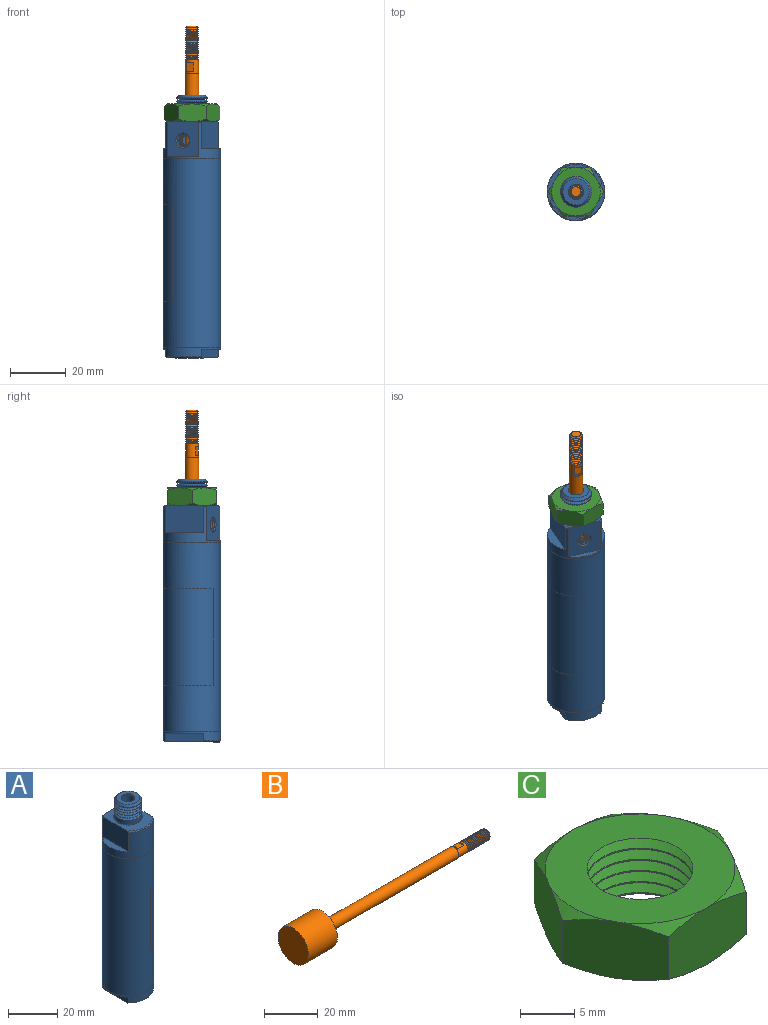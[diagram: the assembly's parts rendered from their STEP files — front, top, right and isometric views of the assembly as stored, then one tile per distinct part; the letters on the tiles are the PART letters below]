
ASSEMBLY  parts=3 mates=4
PART A: 146 faces, bbox 20.7x20.7x94.8 mm
  f0: cylinder r=7.96mm len=54.98mm, axis (0,0,-1), area 2750.9mm2, adj f46,f108
  f1: plane 9.12x9.12mm, normal (0,0,1), area 51.8mm2, adj f2,f11
  f2: cone r=4.7mm half-angle=45deg, axis (0,0,-1), area 11.7mm2, adj f1,f47
  f3: cone r=10.08mm half-angle=45deg, axis (0,0,1), area 9.7mm2, adj f5,f6,f8,f10
  f4: cone r=10.08mm half-angle=45deg, axis (0,0,1), area 9.7mm2, adj f5,f6,f8,f10
  f5: plane 19.72x14mm, normal (0,0,-1), area 226.4mm2, adj f3,f4,f8,f10,f12
  f6: cylinder r=10.31mm len=20.61mm, axis (0,0,-1), area 133.4mm2, adj f3,f4,f7,f8,f9,f10,f117
  f7: plane 15.13x3.31mm, normal (0,0,-1), area 34.6mm2, adj f6,f8
  f8: plane 15.15x3.19mm, normal (-1,0,0), area 47.8mm2, adj f3,f4,f5,f6,f7
  f9: plane 15.13x3.31mm, normal (0,0,-1), area 34.6mm2, adj f6,f10
  f10: plane 15.15x3.19mm, normal (1,0,0), area 47.8mm2, adj f3,f4,f5,f6,f9
  f11: cylinder r=2.07mm len=4.14mm, axis (0,0,1), area 3.1mm2, adj f1,f44
  f12: cone r=2.78mm half-angle=45deg, axis (0,0,-1), area 15.3mm2, adj f5,f13
  f13: cone r=2.37mm half-angle=60deg, axis (0,0,1), area 10.4mm2, adj f12,f14
  f14: cone r=2.37mm half-angle=60deg, axis (0,0,-1), area 10.4mm2, adj f13,f24
  f15: cylinder r=2.07mm len=4.14mm, axis (0,0,1), area 1.1mm2, adj f42,f43
  f16: cylinder r=2.07mm len=4.14mm, axis (0,0,1), area 1.1mm2, adj f40,f41
  f17: cylinder r=2.07mm len=4.14mm, axis (0,0,1), area 1.1mm2, adj f38,f39
  f18: cylinder r=2.07mm len=4.14mm, axis (0,0,1), area 1.1mm2, adj f36,f37
  f19: cylinder r=2.07mm len=4.14mm, axis (0,0,1), area 1.1mm2, adj f34,f35
  f20: cylinder r=2.07mm len=4.14mm, axis (0,0,1), area 1.1mm2, adj f32,f33
  f21: cylinder r=2.07mm len=4.14mm, axis (0,0,1), area 1.1mm2, adj f30,f31
  f22: cylinder r=2.07mm len=4.14mm, axis (0,0,1), area 1.1mm2, adj f28,f29
  f23: cylinder r=2.07mm len=4.14mm, axis (0,0,1), area 1.1mm2, adj f26,f27
  f24: cylinder r=2.07mm len=4.14mm, axis (0,0,1), area 1.1mm2, adj f14,f25
  f25: cone r=2.37mm half-angle=60deg, axis (0,0,1), area 10.4mm2, adj f24,f26
  f26: cone r=2.37mm half-angle=60deg, axis (0,0,-1), area 10.4mm2, adj f23,f25
  f27: cone r=2.37mm half-angle=60deg, axis (0,0,1), area 10.4mm2, adj f23,f28
  f28: cone r=2.37mm half-angle=60deg, axis (0,0,-1), area 10.4mm2, adj f22,f27
  f29: cone r=2.37mm half-angle=60deg, axis (0,0,1), area 10.4mm2, adj f22,f30
  f30: cone r=2.37mm half-angle=60deg, axis (0,0,-1), area 10.4mm2, adj f21,f29
  f31: cone r=2.37mm half-angle=60deg, axis (0,0,1), area 10.4mm2, adj f21,f32
  f32: cone r=2.37mm half-angle=60deg, axis (0,0,-1), area 10.4mm2, adj f20,f31
  f33: cone r=2.37mm half-angle=60deg, axis (0,0,1), area 10.4mm2, adj f20,f34
  f34: cone r=2.37mm half-angle=60deg, axis (0,0,-1), area 10.4mm2, adj f19,f33
  f35: cone r=2.37mm half-angle=60deg, axis (0,0,1), area 10.4mm2, adj f19,f36
  f36: cone r=2.37mm half-angle=60deg, axis (0,0,-1), area 10.4mm2, adj f18,f35
  f37: cone r=2.37mm half-angle=60deg, axis (0,0,1), area 10.4mm2, adj f18,f38
  f38: cone r=2.37mm half-angle=60deg, axis (0,0,-1), area 10.4mm2, adj f17,f37
  f39: cone r=2.37mm half-angle=60deg, axis (0,0,1), area 10.4mm2, adj f17,f40
  f40: cone r=2.37mm half-angle=60deg, axis (0,0,-1), area 10.4mm2, adj f16,f39
  f41: cone r=2.37mm half-angle=60deg, axis (0,0,1), area 10.4mm2, adj f16,f42
  f42: cone r=2.37mm half-angle=60deg, axis (0,0,-1), area 10.4mm2, adj f15,f41
  f43: cone r=2.37mm half-angle=60deg, axis (0,0,1), area 10.4mm2, adj f15,f44
  f44: cone r=2.37mm half-angle=60deg, axis (0,0,-1), area 10.4mm2, adj f11,f43
  f45: plane 15.42x15.42mm, normal (0,0,1), area 113.1mm2, adj f46,f47
  f46: cone r=7.84mm half-angle=30deg, axis (0,0,-1), area 25mm2, adj f0,f45
  f47: cylinder r=4.84mm len=9.68mm, axis (0,0,-1), area 47.1mm2, adj f2,f45
  f48: cylinder r=2.77mm len=5.54mm, axis (0,0,1), area 10mm2, adj f54,f113
  f49: plane 6x6mm, normal (0,0,-1), area 0.1mm2, adj f50,f111
  f50: cylinder r=3mm len=9.84mm, axis (0,0,1), area 185.5mm2, adj f49,f51
  f51: cone r=3.13mm half-angle=45deg, axis (0,0,-1), area 7.1mm2, adj f50,f52
  f52: plane 7.52x7.52mm, normal (0,0,-1), area 11.1mm2, adj f51,f53
  f53: torus R=3.76mm, axis (0,0,1), area 7.8mm2, adj f52,f79
  f54: plane 9.46x9.46mm, normal (0,0,1), area 46.2mm2, adj f48,f55
  f55: cone r=5.14mm half-angle=45deg, axis (0,0,-1), area 37.7mm2, adj f54,f57
  f56: cone r=10.08mm half-angle=45deg, axis (0,0,-1), area 9.9mm2, adj f58,f64,f65,f68
  f57: cylinder r=5.56mm len=11.11mm, axis (0,0,-1), area 12.3mm2, adj f55,f105
  f58: plane 18.12x14.17mm, normal (0,0,1), area 137.2mm2, adj f56,f59,f62,f64,f65,f67,f69
  f59: torus R=5.76mm, axis (0,0,-1), area 11.3mm2, adj f58,f92
  f60: plane 9.12x9.12mm, normal (0,0,-1), area 16mm2, adj f61,f79
  f61: cone r=4.7mm half-angle=45deg, axis (0,0,1), area 11.7mm2, adj f60,f109
  f62: cone r=10.08mm half-angle=45deg, axis (0,0,-1), area 1.1mm2, adj f58,f65,f68,f69
  f63: plane 14.97x3.22mm, normal (0,0,1), area 33.3mm2, adj f64,f68
  f64: plane 14.98x9.9mm, normal (1,0,0), area 147.6mm2, adj f56,f58,f63,f67,f68
  f65: plane 14.98x9.9mm, normal (-1,0,0), area 147.6mm2, adj f56,f58,f62,f66,f68
  f66: plane 14.97x3.22mm, normal (0,0,1), area 33.3mm2, adj f65,f68
  f67: cone r=10.08mm half-angle=45deg, axis (0,0,-1), area 1.1mm2, adj f58,f64,f68,f69
  f68: cylinder r=10.31mm len=20.61mm, axis (0,0,-1), area 364.7mm2, adj f56,f62,f63,f64,f65,f66,f67,f69
  f69: plane 12.72x12.36mm, normal (0,1,0), area 132.1mm2, adj f58,f62,f67,f68,f70,f72
  f70: plane 12.34x2.05mm, normal (0,0,1), area 17.2mm2, adj f68,f69
  f71: cylinder r=2.07mm len=4.14mm, axis (0,-1,0), area 1.1mm2, adj f79,f87,f88,f89
  f72: cone r=2.78mm half-angle=45deg, axis (0,1,0), area 11mm2, adj f69,f73
  f73: cone r=2.37mm half-angle=60deg, axis (0,-1,0), area 6.9mm2, adj f72,f74
  f74: cone r=2.37mm half-angle=60deg, axis (0,1,0), area 10.4mm2, adj f73,f78
  f75: cylinder r=2.07mm len=4.14mm, axis (0,-1,0), area 1.1mm2, adj f85,f86
  f76: cylinder r=2.07mm len=4.14mm, axis (0,-1,0), area 1.1mm2, adj f83,f84
  f77: cylinder r=2.07mm len=4.14mm, axis (0,-1,0), area 1.1mm2, adj f81,f82
  f78: cylinder r=2.07mm len=4.14mm, axis (0,-1,0), area 1.1mm2, adj f74,f80
  f79: cylinder r=3.96mm len=17.7mm, axis (0,0,1), area 423.2mm2, adj f53,f60,f71,f88,f89,f90,f91
  f80: cone r=2.37mm half-angle=60deg, axis (0,-1,0), area 10.4mm2, adj f78,f81
  f81: cone r=2.37mm half-angle=60deg, axis (0,1,0), area 10.4mm2, adj f77,f80
  f82: cone r=2.37mm half-angle=60deg, axis (0,-1,0), area 10.4mm2, adj f77,f83
  f83: cone r=2.37mm half-angle=60deg, axis (0,1,0), area 10.4mm2, adj f76,f82
  f84: cone r=2.37mm half-angle=60deg, axis (0,-1,0), area 10.4mm2, adj f76,f85
  f85: cone r=2.37mm half-angle=60deg, axis (0,1,0), area 10.4mm2, adj f75,f84
  f86: cone r=2.37mm half-angle=60deg, axis (0,-1,0), area 10.4mm2, adj f75,f87
  f87: cone r=2.37mm half-angle=60deg, axis (0,1,0), area 10.4mm2, adj f71,f86
  f88: cone r=2.37mm half-angle=60deg, axis (0,-1,0), area 3.9mm2, adj f71,f79,f90
  f89: cone r=2.37mm half-angle=60deg, axis (0,-1,0), area 3.9mm2, adj f71,f79,f91
  f90: cone r=2.37mm half-angle=60deg, axis (0,1,0), area 1.8mm2, adj f79,f88
  f91: cone r=2.37mm half-angle=60deg, axis (0,1,0), area 1.8mm2, adj f79,f89
  f92: cylinder r=5.56mm len=11.11mm, axis (0,0,-1), area 70.9mm2, adj f59,f94
  f93: cone r=5.08mm half-angle=60deg, axis (0,0,1), area 35.4mm2, adj f94,f98
  f94: cone r=5.08mm half-angle=60deg, axis (0,0,-1), area 35.4mm2, adj f92,f93
  f95: cylinder r=5.56mm len=11.11mm, axis (0,0,-1), area 4.8mm2, adj f103,f106
  f96: cylinder r=5.56mm len=11.11mm, axis (0,0,-1), area 4.8mm2, adj f101,f104
  f97: cylinder r=5.56mm len=11.11mm, axis (0,0,-1), area 4.8mm2, adj f99,f102
  f98: cylinder r=5.56mm len=11.11mm, axis (0,0,-1), area 4.8mm2, adj f93,f100
  f99: cone r=5.08mm half-angle=60deg, axis (0,0,1), area 35.4mm2, adj f97,f100
  f100: cone r=5.08mm half-angle=60deg, axis (0,0,-1), area 35.4mm2, adj f98,f99
  f101: cone r=5.08mm half-angle=60deg, axis (0,0,1), area 35.4mm2, adj f96,f102
  f102: cone r=5.08mm half-angle=60deg, axis (0,0,-1), area 35.4mm2, adj f97,f101
  f103: cone r=5.08mm half-angle=60deg, axis (0,0,1), area 35.4mm2, adj f95,f104
  f104: cone r=5.08mm half-angle=60deg, axis (0,0,-1), area 35.4mm2, adj f96,f103
  f105: cone r=5.08mm half-angle=60deg, axis (0,0,1), area 35.4mm2, adj f57,f106
  f106: cone r=5.08mm half-angle=60deg, axis (0,0,-1), area 35.4mm2, adj f95,f105
  f107: plane 15.42x15.42mm, normal (0,0,-1), area 113.1mm2, adj f108,f109
  f108: cone r=7.84mm half-angle=30deg, axis (0,0,1), area 25mm2, adj f0,f107
  f109: cylinder r=4.84mm len=9.68mm, axis (0,0,1), area 47.1mm2, adj f61,f107
  f110: plane 5.99x5.99mm, normal (0,0,-1), area 8mm2, adj f111,f112
  f111: cylinder r=3mm len=9.53mm, axis (0,0,-1), area 179.4mm2, adj f49,f110
  f112: cylinder r=2.54mm len=9.53mm, axis (0,0,-1), area 152mm2, adj f110,f113
  f113: plane 5.54x5.54mm, normal (0,0,1), area 3.9mm2, adj f48,f112
  f114: cylinder r=10.36mm len=67.82mm, axis (0,0,1), area 3509.3mm2, adj f115,f116,f117
  f115: cylinder r=10.36mm len=34.93mm, axis (0,0,1), area 906.6mm2, adj f114
  f116: plane 20.73x20.73mm, normal (0,0,1), area 3.7mm2, adj f68,f114
  f117: plane 20.73x20.73mm, normal (0,0,-1), area 3.7mm2, adj f6,f114
  f118: plane 18.49x18.49mm, normal (0,0,-1), area 69.3mm2, adj f119,f125
  f119: cylinder r=9.25mm len=59.06mm, axis (0,0,-1), area 3430.6mm2, adj f118,f120
  f120: plane 18.49x18.49mm, normal (0,0,1), area 69.3mm2, adj f119,f130
  f121: cone r=9.61mm half-angle=30deg, axis (0,0,-1), area 16mm2, adj f122,f131
  f122: plane 19.04x19.04mm, normal (0,0,1), area 22mm2, adj f121,f123
  f123: cylinder r=9.14mm len=18.29mm, axis (0,0,-1), area 43.8mm2, adj f122,f124
  f124: plane 18.29x18.29mm, normal (0,0,1), area 63.5mm2, adj f123,f125
  f125: cylinder r=7.96mm len=15.93mm, axis (0,0,-1), area 15.9mm2, adj f118,f124
  f126: plane 19.04x19.04mm, normal (0,0,-1), area 22mm2, adj f127,f128
  f127: cone r=9.61mm half-angle=30deg, axis (0,0,1), area 16mm2, adj f126,f131
  f128: cylinder r=9.14mm len=18.29mm, axis (0,0,1), area 43.8mm2, adj f126,f129
  f129: plane 18.29x18.29mm, normal (0,0,-1), area 63.5mm2, adj f128,f130
  f130: cylinder r=7.96mm len=15.93mm, axis (0,0,1), area 15.9mm2, adj f120,f129
  f131: cylinder r=9.65mm len=61.67mm, axis (0,0,1), area 3740.2mm2, adj f121,f127
  f132: cylinder r=9.65mm len=19.3mm, axis (0,0,1), area 81.1mm2, adj f133,f138
  f133: cone r=9.78mm half-angle=30deg, axis (0,0,1), area 31.2mm2, adj f132,f139
  f134: torus R=9.33mm, axis (0,0,1), area 15.1mm2, adj f135,f136
  f135: cylinder r=9.13mm len=18.26mm, axis (0,0,-1), area 72.2mm2, adj f134,f137
  f136: cone r=9.42mm half-angle=74deg, axis (0,0,1), area 26.3mm2, adj f134,f139
  f137: torus R=9.33mm, axis (0,0,-1), area 18.5mm2, adj f135,f138
  f138: plane 19.3x19.3mm, normal (0,0,1), area 18.9mm2, adj f132,f137
  f139: plane 19.81x19.81mm, normal (0,0,-1), area 12.5mm2, adj f133,f136
  f140: cylinder r=9.65mm len=19.3mm, axis (0,0,1), area 81.1mm2, adj f141,f145
  f141: cone r=9.78mm half-angle=30deg, axis (0,0,-1), area 31.2mm2, adj f140,f144
  f142: cone r=9.42mm half-angle=74deg, axis (0,0,-1), area 35.2mm2, adj f143,f144
  f143: cylinder r=9.13mm len=18.26mm, axis (0,0,-1), area 92.6mm2, adj f142,f145
  f144: plane 19.81x19.81mm, normal (0,0,1), area 12.5mm2, adj f141,f142
  f145: plane 19.3x19.3mm, normal (0,0,-1), area 30.7mm2, adj f140,f143
PART B: 59 faces, bbox 101.7x15.9x15.9 mm
  f0: cone r=2.06mm half-angle=60deg, axis (1,0,0), area 9mm2, adj f1,f43
  f1: cone r=2.06mm half-angle=60deg, axis (-1,0,0), area 9mm2, adj f0,f49
  f2: cone r=2.06mm half-angle=60deg, axis (1,0,0), area 9mm2, adj f3,f42
  f3: cone r=2.06mm half-angle=60deg, axis (-1,0,0), area 9mm2, adj f2,f43
  f4: cone r=2.06mm half-angle=60deg, axis (1,0,0), area 9mm2, adj f5,f41
  f5: cone r=2.06mm half-angle=60deg, axis (-1,0,0), area 9mm2, adj f4,f42
  f6: cone r=2.06mm half-angle=60deg, axis (1,0,0), area 9mm2, adj f7,f40
  f7: cone r=2.06mm half-angle=60deg, axis (-1,0,0), area 9mm2, adj f6,f41
  f8: cone r=2.06mm half-angle=60deg, axis (1,0,0), area 9mm2, adj f9,f39
  f9: cone r=2.06mm half-angle=60deg, axis (-1,0,0), area 9mm2, adj f8,f40
  f10: cone r=2.06mm half-angle=60deg, axis (1,0,0), area 9mm2, adj f11,f38
  f11: cone r=2.06mm half-angle=60deg, axis (-1,0,0), area 9mm2, adj f10,f39
  f12: cone r=2.06mm half-angle=60deg, axis (1,0,0), area 9mm2, adj f13,f37
  f13: cone r=2.06mm half-angle=60deg, axis (-1,0,0), area 9mm2, adj f12,f38
  f14: cone r=2.06mm half-angle=60deg, axis (1,0,0), area 9mm2, adj f15,f36
  f15: cone r=2.06mm half-angle=60deg, axis (-1,0,0), area 9mm2, adj f14,f37
  f16: cone r=2.06mm half-angle=60deg, axis (1,0,0), area 9mm2, adj f17,f35
  f17: cone r=2.06mm half-angle=60deg, axis (-1,0,0), area 9mm2, adj f16,f36
  f18: cone r=2.06mm half-angle=60deg, axis (1,0,0), area 9mm2, adj f19,f34
  f19: cone r=2.06mm half-angle=60deg, axis (-1,0,0), area 9mm2, adj f18,f35
  f20: cone r=2.06mm half-angle=60deg, axis (1,0,0), area 9mm2, adj f21,f33
  f21: cone r=2.06mm half-angle=60deg, axis (-1,0,0), area 9mm2, adj f20,f34
  f22: cone r=2.06mm half-angle=60deg, axis (1,0,0), area 9mm2, adj f23,f32
  f23: cone r=2.06mm half-angle=60deg, axis (-1,0,0), area 9mm2, adj f22,f33
  f24: cone r=2.06mm half-angle=60deg, axis (1,0,0), area 9mm2, adj f25,f31
  f25: cone r=2.06mm half-angle=60deg, axis (-1,0,0), area 9mm2, adj f24,f32
  f26: cone r=2.06mm half-angle=60deg, axis (1,0,0), area 9mm2, adj f27,f30
  f27: cone r=2.06mm half-angle=60deg, axis (-1,0,0), area 9mm2, adj f26,f31
  f28: cone r=2.06mm half-angle=60deg, axis (1,0,0), area 7.5mm2, adj f29,f48
  f29: cone r=2.06mm half-angle=60deg, axis (-1,0,0), area 9mm2, adj f28,f30
  f30: cylinder r=2.36mm len=4.72mm, axis (1,0,0), area 1.3mm2, adj f26,f29
  f31: cylinder r=2.36mm len=4.72mm, axis (1,0,0), area 1.3mm2, adj f24,f27
  f32: cylinder r=2.36mm len=4.72mm, axis (1,0,0), area 1.3mm2, adj f22,f25
  f33: cylinder r=2.36mm len=4.72mm, axis (1,0,0), area 1.3mm2, adj f20,f23
  f34: cylinder r=2.36mm len=4.72mm, axis (1,0,0), area 1.3mm2, adj f18,f21
  f35: cylinder r=2.36mm len=4.72mm, axis (1,0,0), area 1.3mm2, adj f16,f19
  f36: cylinder r=2.36mm len=4.72mm, axis (1,0,0), area 1.3mm2, adj f14,f17
  f37: cylinder r=2.36mm len=4.72mm, axis (1,0,0), area 1.3mm2, adj f12,f15
  f38: cylinder r=2.36mm len=4.72mm, axis (1,0,0), area 1.3mm2, adj f10,f13
  f39: cylinder r=2.36mm len=4.72mm, axis (1,0,0), area 1.3mm2, adj f8,f11
  f40: cylinder r=2.36mm len=4.72mm, axis (1,0,0), area 1.3mm2, adj f6,f9
  f41: cylinder r=2.36mm len=4.72mm, axis (1,0,0), area 1.3mm2, adj f4,f7
  f42: cylinder r=2.36mm len=4.72mm, axis (1,0,0), area 1.3mm2, adj f2,f5
  f43: cylinder r=2.36mm len=4.72mm, axis (1,0,0), area 1.3mm2, adj f0,f3
  f44: cone r=2.06mm half-angle=60deg, axis (-1,0,0), area 0.9mm2, adj f48,f50
  f45: plane 15.93x15.93mm, normal (1,0,0), area 179.5mm2, adj f46,f57
  f46: cylinder r=7.96mm len=15.93mm, axis (1,0,0), area 768.8mm2, adj f45,f47
  f47: plane 15.93x15.93mm, normal (-1,0,0), area 199.2mm2, adj f46
  f48: cone r=2.08mm half-angle=45deg, axis (-1,0,0), area 8.1mm2, adj f28,f44
  f49: cylinder r=2.36mm len=4.95mm, axis (1,0,0), area 55.8mm2, adj f1,f51,f52,f53,f54,f55,f56,f58
  f50: plane 3.52x3.52mm, normal (1,0,0), area 9.7mm2, adj f44
  f51: plane 2.63x0.4mm, normal (-1,0,0), area 0.7mm2, adj f49,f53
  f52: plane 2.63x0.4mm, normal (1,0,0), area 0.7mm2, adj f49,f53
  f53: plane 3.18x2.63mm, normal (0,0,1), area 8.4mm2, adj f49,f51,f52
  f54: plane 2.63x0.4mm, normal (1,0,0), area 0.7mm2, adj f49,f56
  f55: plane 2.63x0.4mm, normal (-1,0,0), area 0.7mm2, adj f49,f56
  f56: plane 3.18x2.63mm, normal (0,0,-1), area 8.4mm2, adj f49,f54,f55
  f57: cylinder r=2.5mm len=69.34mm, axis (1,0,0), area 1089.7mm2, adj f45,f58
  f58: plane 5x5mm, normal (1,0,0), area 2.1mm2, adj f49,f57
PART C: 36 faces, bbox 20.2x20.2x6.4 mm
  f0: cone r=5.35mm half-angle=60deg, axis (0,0,-1), area 6.2mm2, adj f31,f32
  f1: cone r=5.35mm half-angle=60deg, axis (0,0,1), area 37.3mm2, adj f2,f31
  f2: cone r=5.35mm half-angle=60deg, axis (0,0,-1), area 37.3mm2, adj f1,f12
  f3: cone r=5.35mm half-angle=60deg, axis (0,0,1), area 37.3mm2, adj f4,f12
  f4: cone r=5.35mm half-angle=60deg, axis (0,0,-1), area 37.3mm2, adj f3,f11
  f5: cone r=5.35mm half-angle=60deg, axis (0,0,1), area 37.3mm2, adj f6,f11
  f6: cone r=5.35mm half-angle=60deg, axis (0,0,-1), area 37.3mm2, adj f5,f10
  f7: cone r=5.35mm half-angle=60deg, axis (0,0,1), area 37.3mm2, adj f8,f10
  f8: cone r=5.35mm half-angle=60deg, axis (0,0,-1), area 37.3mm2, adj f7,f9
  f9: cylinder r=4.86mm len=9.73mm, axis (0,0,-1), area 4.2mm2, adj f8,f13
  f10: cylinder r=4.86mm len=9.73mm, axis (0,0,-1), area 4.2mm2, adj f6,f7
  f11: cylinder r=4.86mm len=9.73mm, axis (0,0,-1), area 4.2mm2, adj f4,f5
  f12: cylinder r=4.86mm len=9.73mm, axis (0,0,-1), area 4.2mm2, adj f2,f3
  f13: cone r=5.35mm half-angle=60deg, axis (0,0,1), area 37.3mm2, adj f9,f14
  f14: cone r=5.35mm half-angle=60deg, axis (0,0,-1), area 37.3mm2, adj f13,f35
  f15: cone r=9.41mm half-angle=60deg, axis (0,0,1), area 4.7mm2, adj f29,f30,f32
  f16: cone r=9.41mm half-angle=60deg, axis (0,0,1), area 4.7mm2, adj f29,f32,f34
  f17: cone r=9.41mm half-angle=60deg, axis (0,0,1), area 4.7mm2, adj f28,f30,f32
  f18: cone r=9.41mm half-angle=60deg, axis (0,0,1), area 4.7mm2, adj f32,f33,f34
  f19: cone r=9.41mm half-angle=60deg, axis (0,0,1), area 4.7mm2, adj f27,f28,f32
  f20: cone r=9.41mm half-angle=60deg, axis (0,0,1), area 4.7mm2, adj f27,f32,f33
  f21: cone r=9.41mm half-angle=60deg, axis (0,0,-1), area 4.7mm2, adj f28,f30,f35
  f22: cone r=9.41mm half-angle=60deg, axis (0,0,-1), area 4.7mm2, adj f29,f30,f35
  f23: cone r=9.41mm half-angle=60deg, axis (0,0,-1), area 4.7mm2, adj f29,f34,f35
  f24: cone r=9.41mm half-angle=60deg, axis (0,0,-1), area 4.7mm2, adj f27,f28,f35
  f25: cone r=9.41mm half-angle=60deg, axis (0,0,-1), area 4.7mm2, adj f33,f34,f35
  f26: cone r=9.41mm half-angle=60deg, axis (0,0,-1), area 4.7mm2, adj f27,f33,f35
  f27: plane 8.73x6.35mm, normal (0.87,-0.5,0), area 58.6mm2, adj f19,f20,f24,f26,f28,f33
  f28: plane 8.73x6.35mm, normal (0.87,0.5,0), area 58.6mm2, adj f17,f19,f21,f24,f27,f30
  f29: plane 8.73x6.35mm, normal (-0.87,0.5,0), area 58.6mm2, adj f15,f16,f22,f23,f30,f34
  f30: plane 10.08x6.35mm, normal (0,1,0), area 58.6mm2, adj f15,f17,f21,f22,f28,f29
  f31: cylinder r=4.86mm len=9.73mm, axis (0,0,-1), area 4.2mm2, adj f0,f1
  f32: plane 17.46x17.46mm, normal (0,0,-1), area 159.8mm2, adj f0,f15,f16,f17,f18,f19,f20
  f33: plane 10.08x6.35mm, normal (0,-1,0), area 58.6mm2, adj f18,f20,f25,f26,f27,f34
  f34: plane 8.73x6.35mm, normal (-0.87,-0.5,0), area 58.6mm2, adj f16,f18,f23,f25,f29,f33
  f35: plane 17.46x17.46mm, normal (0,0,1), area 165.2mm2, adj f14,f21,f22,f23,f24,f25,f26
PLACE A rot(axis=(0,0,1),156.5deg) t=(-21.8,6.19,40.92)mm
PLACE B rot(axis=(0.49,-0.72,0.49),108.2deg) t=(-21.8,6.19,30.64)mm
PLACE C t=(-21.8,6.19,91.47)mm
MATE parallel B.f44 <-> A.f16  axis (0,0,1) through (-21.8,6.19,105.7)mm
MATE planar A.f58 <-> C.f32  axis (0,0,1) through (-25.09,-1.38,88.29)mm
MATE cylindrical B.f57 <-> A.f16  axis (0,0,1) through (-21.8,6.19,71.03)mm
MATE cylindrical A.f16 <-> C.f0  axis (0,0,-1) through (-21.8,6.19,88.5)mm
